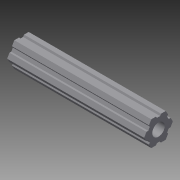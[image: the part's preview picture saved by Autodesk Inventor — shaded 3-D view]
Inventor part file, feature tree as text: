
AUTODESK INVENTOR PART (.ipt)
format: ipt  version: 2015 SP1 (Build 190203100, 203)  size: 153,088 bytes
history: native  units: in
note: dims shown in document units (in); Inventor stores cm internally (conversion verified against a paired STEP export)
features: extrude x1, sketch x1
ambient origin geometry x8: Origin, YZ Plane, XZ Plane, XY Plane, X Axis, Y Axis, Z Axis, Center Point
bodies: Solid1 (feature_tree)
feature tree (2):
  extrude  "Extrusion1"  Depth=0.5in
  sketch  "Sketch1"  dims[d0=0.5in d1=0.5in d2=0.5in d3=120.0deg d4=120.0deg d5=0.25in d6=0.25in d7=0.25in d11=0.0312in d12=0.0938in d13=0.0938in d14=0.0938in d15=0.0938in d16=0.0938in d17=0.0938in d18=0.0938in d19=0.0938in d20=0.0938in d21=0.0938in d22=0.0938in d23=0.0938in d24=150.0deg d25=150.0deg d26=150.0deg d27=90.0deg d28=90.0deg d29=30.0deg d30=30.0deg d31=30.0deg d32=30.0deg d33=90.0deg d34=90.0deg d35=150.0deg d36=0.25in d37=2.75in d38=0.0in]
